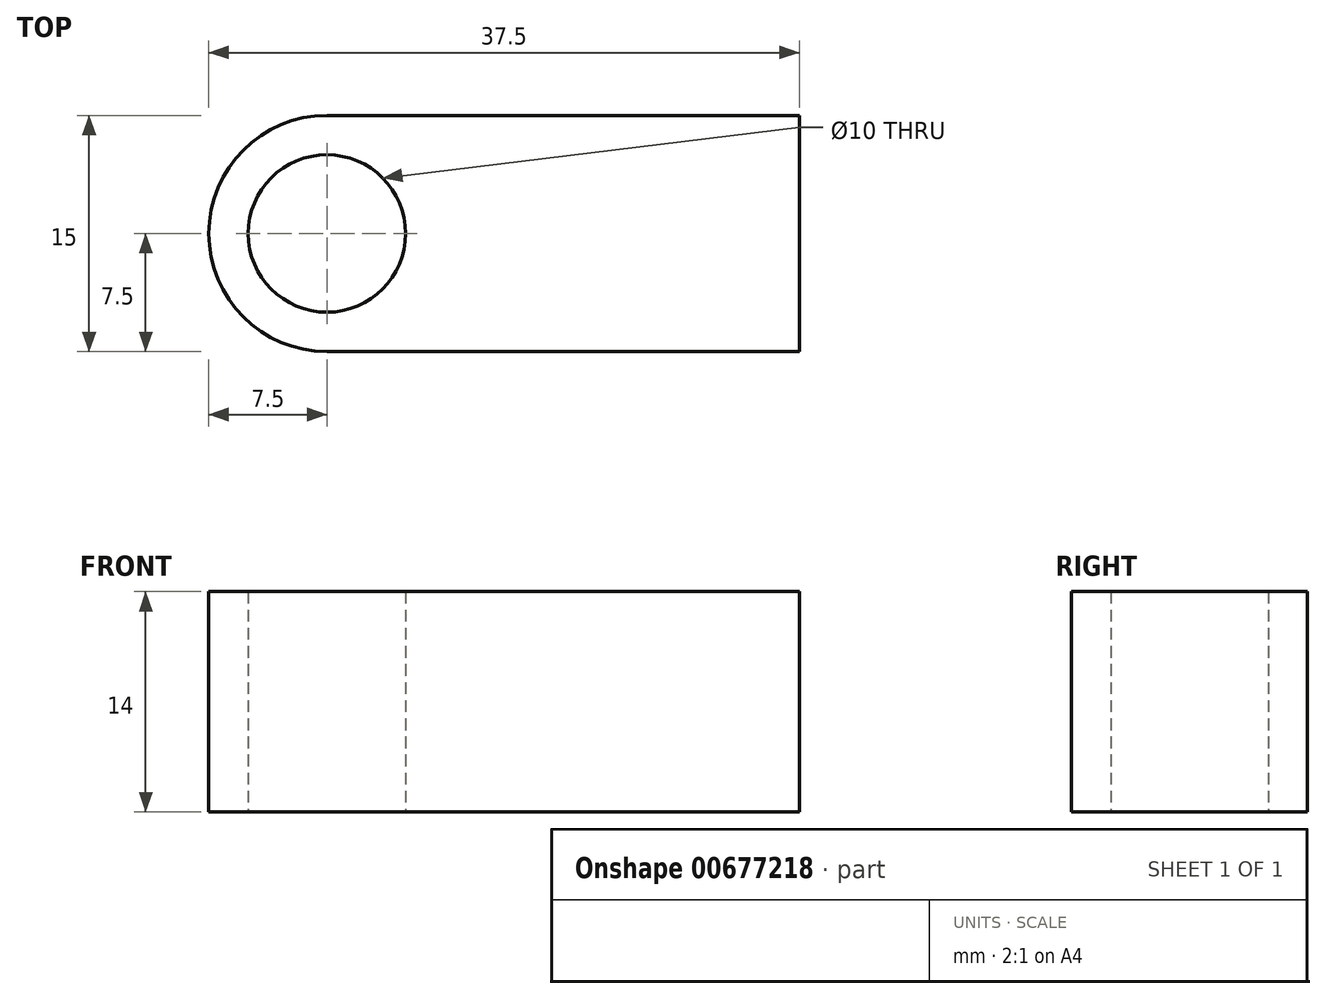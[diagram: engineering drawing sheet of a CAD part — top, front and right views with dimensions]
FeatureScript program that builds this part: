
annotation { "Feature Type Name" : "Feature", "Feature Type Description" : "" }
export const myFeature = defineFeature(function(context is Context, id is Id, definition is map)
    precondition{}
    {
        {
            var Q0;
            Q0=qCreatedBy(makeId("Top.planeOp"),FACE);
            var sketch = newSketch(context, id + "F0", { "sketchPlane" : qUnion([Q0])});
            skLineSegment(sketch, "E0.bottom", {"start": v(-15, -7.5) * mm, "end": v(15, -7.5) * mm});
            skLineSegment(sketch, "E0.top", {"start": v(-15, 7.5) * mm, "end": v(15, 7.5) * mm});
            skLineSegment(sketch, "E0.left", {"start": v(-15, -7.5) * mm, "end": v(-15, 7.5) * mm});
            skLineSegment(sketch, "E0.right", {"start": v(15, -7.5) * mm, "end": v(15, 7.5) * mm});
            skPoint(sketch, "E0.middle", {"position": v(0, 0) * mm});
            skArc(sketch, "E1", {"start": v(15, -7.5) * mm, "mid": v(22.5, 0) * mm, "end": v(15, 7.5) * mm});
            skCircle(sketch, "E2", {"center": v(15, 0) * mm, "radius": 5 * mm});
            skPoint(sketch, "E3.middle.positionSnap0", {"position": v(22.5, 0) * mm});
            skLineSegment(sketch, "E4.bottom", {"start": v(15, 7.5) * mm, "end": v(45, 7.5) * mm});
            skLineSegment(sketch, "E4.top", {"start": v(15, -7.5) * mm, "end": v(45, -7.5) * mm});
            skLineSegment(sketch, "E4.left", {"start": v(15, 7.5) * mm, "end": v(15, -7.5) * mm});
            skLineSegment(sketch, "E4.right", {"start": v(45, 7.5) * mm, "end": v(45, -7.5) * mm});
            skArc(sketch, "E5", {"start": v(15, 7.5) * mm, "mid": v(7.5, 0) * mm, "end": v(15, -7.5) * mm});
            skSolve(sketch);
        }
        {
            var Q0;
            Q0=makeQuery(id+"F0.imprint","IMPRINT",FACE,{"disambiguationData":[TD([[makeQuery(id+"F0.imprint","IMPRINT",EDGE,{"derivedFrom":sQuery(id+"F0.wireOp",EDGE,"E1")}),-1.0]])]});
            var Q1;
            {var subQ4=sQuery(id+"F0.wireOp",EDGE,"E5");Q1=makeQuery(id+"F0.imprint","IMPRINT",FACE,{"disambiguationData":[TD([[makeQuery(id+"F0.imprint","IMPRINT",EDGE,{"derivedFrom":subQ4}),1.0]])]});}
            var Q2;
            {var subQ0=sQuery(id+"F0.wireOp",EDGE,"E1");Q2=makeQuery(id+"F0.imprint","IMPRINT",FACE,{"disambiguationData":[TD([[makeQuery(id+"F0.imprint","IMPRINT",EDGE,{"derivedFrom":subQ0}),1.0]])]});}
            extrude(context, id + "F1", {"entities" : qUnion([Q0, Q1, Q2]), "depth" : 14 * mm, "offsetDistance" : 25 * mm});
        }
    });
